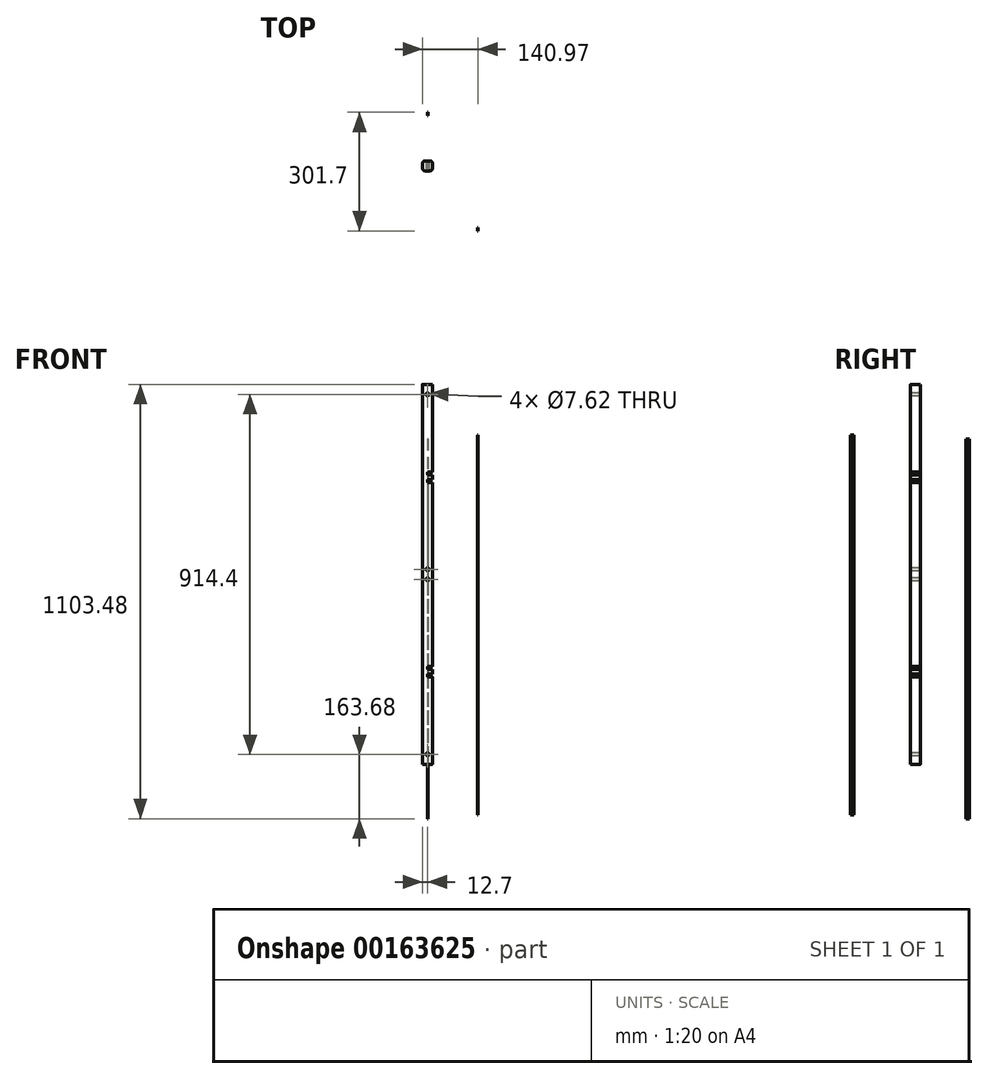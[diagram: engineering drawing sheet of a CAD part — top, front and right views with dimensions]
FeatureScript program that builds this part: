
annotation { "Feature Type Name" : "Feature", "Feature Type Description" : "" }
export const myFeature = defineFeature(function(context is Context, id is Id, definition is map)
    precondition{}
    {
        {
            var Q0;
            Q0=qCreatedBy(makeId("Top.planeOp"),FACE);
            var sketch = newSketch(context, id + "F0", { "sketchPlane" : qUnion([Q0])});
            skLineSegment(sketch, "E0.bottom", {"start": v(6.35, 12.7) * mm, "end": v(-6.35, 12.7) * mm});
            skLineSegment(sketch, "E0.top", {"start": v(6.35, -12.7) * mm, "end": v(-6.35, -12.7) * mm});
            skLineSegment(sketch, "E0.left", {"start": v(12.7, 6.35) * mm, "end": v(12.7, -6.35) * mm});
            skLineSegment(sketch, "E0.right", {"start": v(-12.7, 6.35) * mm, "end": v(-12.7, -6.35) * mm});
            skPoint(sketch, "E0.middle", {"position": v(0, 0) * mm});
            skPoint(sketch, "E1.visualSharp", {"position": v(-12.7, 12.7) * mm});
            skArc(sketch, "E1.filletArc", {"start": v(-6.35, 12.7) * mm, "mid": v(-10.84, 10.84) * mm, "end": v(-12.7, 6.35) * mm});
            skPoint(sketch, "E2.visualSharp", {"position": v(-12.7, -12.7) * mm});
            skArc(sketch, "E2.filletArc", {"start": v(-12.7, -6.35) * mm, "mid": v(-10.84, -10.84) * mm, "end": v(-6.35, -12.7) * mm});
            skPoint(sketch, "E3.visualSharp", {"position": v(12.7, -12.7) * mm});
            skArc(sketch, "E3.filletArc", {"start": v(6.35, -12.7) * mm, "mid": v(10.84, -10.84) * mm, "end": v(12.7, -6.35) * mm});
            skPoint(sketch, "E4.visualSharp", {"position": v(12.7, 12.7) * mm});
            skArc(sketch, "E4.filletArc", {"start": v(12.7, 6.35) * mm, "mid": v(10.84, 10.84) * mm, "end": v(6.35, 12.7) * mm});
            skSolve(sketch);
        }
        {
            var Q0;
            Q0=qSketchRegion(id+"F0",true);
            extrude(context, id + "F1", {"entities" : qUnion([Q0]), "depth" : 965.2 * mm});
        }
        {
            var Q0;
            Q0=qCreatedBy(makeId("Right.planeOp"),FACE);
            var sketch = newSketch(context, id + "F2", { "sketchPlane" : qUnion([Q0])});
            skLineSegment(sketch, "E5.bottom", {"start": v(-165.43, 836.7) * mm, "end": v(-156.96, 836.7) * mm});
            skLineSegment(sketch, "E5.top", {"start": v(-165.43, -128.5) * mm, "end": v(-156.96, -128.5) * mm});
            skLineSegment(sketch, "E5.left", {"start": v(-165.43, 836.7) * mm, "end": v(-165.43, -128.5) * mm});
            skLineSegment(sketch, "E5.right", {"start": v(-156.96, 836.7) * mm, "end": v(-156.96, -128.5) * mm});
            skSolve(sketch);
        }
        {
            var Q0;
            Q0=qSketchRegion(id+"F2",true);
            extrude(context, id + "F3", {"entities" : qUnion([Q0]), "depth" : 1.27 * mm});
        }
        {
            var Q0;
            Q0=qCreatedBy(makeId("Right.planeOp"),FACE);
            var sketch = newSketch(context, id + "F4", { "sketchPlane" : qUnion([Q0])});
            skLineSegment(sketch, "E6.bottom", {"start": v(127.8, 826.92) * mm, "end": v(136.27, 826.92) * mm});
            skLineSegment(sketch, "E6.top", {"start": v(127.8, -138.28) * mm, "end": v(136.27, -138.28) * mm});
            skLineSegment(sketch, "E6.left", {"start": v(127.8, 826.92) * mm, "end": v(127.8, -138.28) * mm});
            skLineSegment(sketch, "E6.right", {"start": v(136.27, 826.92) * mm, "end": v(136.27, -138.28) * mm});
            skSolve(sketch);
        }
        {
            var Q0;
            Q0=qSketchRegion(id+"F4",true);
            extrude(context, id + "F5", {"entities" : qUnion([Q0]), "depth" : 1.27 * mm});
        }
        {
            var Q0;
            Q0=makeQuery(id+"F1.opExtrude","SWEPT_FACE",FACE,{"disambiguationData":[OSD([sQuery(id+"F0.wireOp",EDGE,"E0.left")])]});
            var sketch = newSketch(context, id + "F6", { "sketchPlane" : qUnion([Q0])});
            skLineSegment(sketch, "E7", {"start": v(0, 0) * mm, "end": v(0, 965.2) * mm});
            skLineSegment(sketch, "E8", {"start": v(0, 742.95) * mm, "end": v(12.7, 742.95) * mm});
            skLineSegment(sketch, "E9", {"start": v(0, 723.9) * mm, "end": v(12.7, 723.9) * mm});
            skLineSegment(sketch, "E10", {"start": v(0, 222.25) * mm, "end": v(12.7, 222.25) * mm});
            skLineSegment(sketch, "E11", {"start": v(0, 241.3) * mm, "end": v(12.7, 241.3) * mm});
            skLineSegment(sketch, "E12.bottom", {"start": v(12.7, 222.25) * mm, "end": v(-12.7, 222.25) * mm});
            skLineSegment(sketch, "E12.top", {"start": v(12.7, 229.87) * mm, "end": v(-12.7, 229.87) * mm});
            skLineSegment(sketch, "E12.left", {"start": v(12.7, 222.25) * mm, "end": v(12.7, 229.87) * mm});
            skLineSegment(sketch, "E12.right", {"start": v(-12.7, 222.25) * mm, "end": v(-12.7, 229.87) * mm});
            skLineSegment(sketch, "E13.bottom", {"start": v(12.7, 241.3) * mm, "end": v(-12.7, 241.3) * mm});
            skLineSegment(sketch, "E13.top", {"start": v(12.7, 248.92) * mm, "end": v(-12.7, 248.92) * mm});
            skLineSegment(sketch, "E13.left", {"start": v(12.7, 241.3) * mm, "end": v(12.7, 248.92) * mm});
            skLineSegment(sketch, "E13.right", {"start": v(-12.7, 241.3) * mm, "end": v(-12.7, 248.92) * mm});
            skLineSegment(sketch, "E14.bottom", {"start": v(12.7, 742.95) * mm, "end": v(-12.7, 742.95) * mm});
            skLineSegment(sketch, "E14.top", {"start": v(12.7, 735.33) * mm, "end": v(-12.7, 735.33) * mm});
            skLineSegment(sketch, "E14.left", {"start": v(12.7, 742.95) * mm, "end": v(12.7, 735.33) * mm});
            skLineSegment(sketch, "E14.right", {"start": v(-12.7, 742.95) * mm, "end": v(-12.7, 735.33) * mm});
            skLineSegment(sketch, "E15.bottom", {"start": v(12.7, 723.9) * mm, "end": v(-12.7, 723.9) * mm});
            skLineSegment(sketch, "E15.top", {"start": v(12.7, 716.28) * mm, "end": v(-12.7, 716.28) * mm});
            skLineSegment(sketch, "E15.left", {"start": v(12.7, 723.9) * mm, "end": v(12.7, 716.28) * mm});
            skLineSegment(sketch, "E15.right", {"start": v(-12.7, 723.9) * mm, "end": v(-12.7, 716.28) * mm});
            skSolve(sketch);
        }
        {
            var Q0;
            {var subQ0=sQuery(id+"F6.wireOp",EDGE,"E14.right");Q0=makeQuery(id+"F6.imprint","IMPRINT",FACE,{"disambiguationData":[TD([[makeQuery(id+"F6.imprint","IMPRINT",EDGE,{"derivedFrom":subQ0}),1.0]])]});}
            var Q1;
            {var subQ0=sQuery(id+"F6.wireOp",EDGE,"E14.top");var subQ1=sQuery(id+"F6.wireOp",EDGE,"E7");var subQ2=makeQuery(id+"F6.imprint","INTERSECT",VERTEX,{"derivedFrom":[subQ1,subQ0]});Q1=makeQuery(id+"F6.imprint","IMPRINT",FACE,{"disambiguationData":[TD([[makeQuery(id+"F6.imprint","IMPRINT",EDGE,{"disambiguationData":[TD([[subQ2,-1.0]])],"derivedFrom":subQ1}),1.0]])]});}
            var Q2;
            {var subQ0=sQuery(id+"F6.wireOp",EDGE,"E14.top");var subQ1=sQuery(id+"F6.wireOp",EDGE,"E7");var subQ2=makeQuery(id+"F6.imprint","INTERSECT",VERTEX,{"derivedFrom":[subQ1,subQ0]});Q2=makeQuery(id+"F6.imprint","IMPRINT",FACE,{"disambiguationData":[TD([[makeQuery(id+"F6.imprint","IMPRINT",EDGE,{"disambiguationData":[TD([[subQ2,-1.0]])],"derivedFrom":subQ1}),-1.0]])]});}
            var Q3;
            {var subQ0=sQuery(id+"F6.wireOp",EDGE,"E14.left");Q3=makeQuery(id+"F6.imprint","IMPRINT",FACE,{"disambiguationData":[TD([[makeQuery(id+"F6.imprint","IMPRINT",EDGE,{"derivedFrom":subQ0}),-1.0]])]});}
            var Q4;
            {var subQ0=sQuery(id+"F6.wireOp",EDGE,"E15.left");Q4=makeQuery(id+"F6.imprint","IMPRINT",FACE,{"disambiguationData":[TD([[makeQuery(id+"F6.imprint","IMPRINT",EDGE,{"derivedFrom":subQ0}),-1.0]])]});}
            var Q5;
            {var subQ0=sQuery(id+"F6.wireOp",EDGE,"E15.top");var subQ1=sQuery(id+"F6.wireOp",EDGE,"E7");var subQ2=makeQuery(id+"F6.imprint","INTERSECT",VERTEX,{"derivedFrom":[subQ1,subQ0]});Q5=makeQuery(id+"F6.imprint","IMPRINT",FACE,{"disambiguationData":[TD([[makeQuery(id+"F6.imprint","IMPRINT",EDGE,{"disambiguationData":[TD([[subQ2,-1.0]])],"derivedFrom":subQ1}),-1.0]])]});}
            var Q6;
            {var subQ0=sQuery(id+"F6.wireOp",EDGE,"E15.top");var subQ1=sQuery(id+"F6.wireOp",EDGE,"E7");var subQ2=makeQuery(id+"F6.imprint","INTERSECT",VERTEX,{"derivedFrom":[subQ1,subQ0]});Q6=makeQuery(id+"F6.imprint","IMPRINT",FACE,{"disambiguationData":[TD([[makeQuery(id+"F6.imprint","IMPRINT",EDGE,{"disambiguationData":[TD([[subQ2,-1.0]])],"derivedFrom":subQ1}),1.0]])]});}
            var Q7;
            {var subQ0=sQuery(id+"F6.wireOp",EDGE,"E15.right");Q7=makeQuery(id+"F6.imprint","IMPRINT",FACE,{"disambiguationData":[TD([[makeQuery(id+"F6.imprint","IMPRINT",EDGE,{"derivedFrom":subQ0}),1.0]])]});}
            var Q8;
            Q8=sQuery(id+"F6.wireOp",EDGE,"E14.left");
            var Q9;
            Q9=sQuery(id+"F6.wireOp",EDGE,"E8");
            var Q10;
            Q10=sQuery(id+"F6.wireOp",EDGE,"E14.bottom");
            var Q11;
            Q11=sQuery(id+"F6.wireOp",EDGE,"E14.top");
            var Q12;
            Q12=sQuery(id+"F6.wireOp",EDGE,"E14.right");
            var Q13;
            Q13=sQuery(id+"F6.wireOp",EDGE,"E15.bottom");
            var Q14;
            Q14=sQuery(id+"F6.wireOp",EDGE,"E15.top");
            var Q15;
            Q15=sQuery(id+"F6.wireOp",EDGE,"E15.left");
            var Q16;
            Q16=sQuery(id+"F6.wireOp",EDGE,"E15.right");
            extrude(context, id + "F7", {"entities" : qUnion([Q0, Q1, Q2, Q3, Q4, Q5, Q6, Q7]), "operationType" : NewBodyOperationType.REMOVE, "surfaceEntities" : qUnion([Q8, Q9, Q10, Q11, Q12, Q13, Q14, Q15, Q16]), "oppositeDirection" : true, "depth" : 12.7 * mm});
        }
        {
            var Q0;
            {var subQ0=sQuery(id+"F6.wireOp",EDGE,"E13.right");Q0=makeQuery(id+"F6.imprint","IMPRINT",FACE,{"disambiguationData":[TD([[makeQuery(id+"F6.imprint","IMPRINT",EDGE,{"derivedFrom":subQ0}),-1.0]])]});}
            var Q1;
            {var subQ0=sQuery(id+"F6.wireOp",EDGE,"E13.bottom");var subQ1=sQuery(id+"F6.wireOp",EDGE,"E7");var subQ2=makeQuery(id+"F6.imprint","INTERSECT",VERTEX,{"derivedFrom":[subQ1,subQ0]});Q1=makeQuery(id+"F6.imprint","IMPRINT",FACE,{"disambiguationData":[TD([[makeQuery(id+"F6.imprint","IMPRINT",EDGE,{"disambiguationData":[TD([[subQ2,-1.0]])],"derivedFrom":subQ1}),1.0]])]});}
            var Q2;
            {var subQ0=sQuery(id+"F6.wireOp",EDGE,"E13.bottom");var subQ1=sQuery(id+"F6.wireOp",EDGE,"E7");var subQ2=makeQuery(id+"F6.imprint","INTERSECT",VERTEX,{"derivedFrom":[subQ1,subQ0]});Q2=makeQuery(id+"F6.imprint","IMPRINT",FACE,{"disambiguationData":[TD([[makeQuery(id+"F6.imprint","IMPRINT",EDGE,{"disambiguationData":[TD([[subQ2,-1.0]])],"derivedFrom":subQ1}),-1.0]])]});}
            var Q3;
            {var subQ0=sQuery(id+"F6.wireOp",EDGE,"E13.left");Q3=makeQuery(id+"F6.imprint","IMPRINT",FACE,{"disambiguationData":[TD([[makeQuery(id+"F6.imprint","IMPRINT",EDGE,{"derivedFrom":subQ0}),1.0]])]});}
            var Q4;
            {var subQ0=sQuery(id+"F6.wireOp",EDGE,"E12.left");Q4=makeQuery(id+"F6.imprint","IMPRINT",FACE,{"disambiguationData":[TD([[makeQuery(id+"F6.imprint","IMPRINT",EDGE,{"derivedFrom":subQ0}),1.0]])]});}
            var Q5;
            {var subQ0=sQuery(id+"F6.wireOp",EDGE,"E12.bottom");var subQ1=sQuery(id+"F6.wireOp",EDGE,"E7");var subQ2=makeQuery(id+"F6.imprint","INTERSECT",VERTEX,{"derivedFrom":[subQ1,subQ0]});Q5=makeQuery(id+"F6.imprint","IMPRINT",FACE,{"disambiguationData":[TD([[makeQuery(id+"F6.imprint","IMPRINT",EDGE,{"disambiguationData":[TD([[subQ2,-1.0]])],"derivedFrom":subQ1}),-1.0]])]});}
            var Q6;
            {var subQ0=sQuery(id+"F6.wireOp",EDGE,"E12.bottom");var subQ1=sQuery(id+"F6.wireOp",EDGE,"E7");var subQ2=makeQuery(id+"F6.imprint","INTERSECT",VERTEX,{"derivedFrom":[subQ1,subQ0]});Q6=makeQuery(id+"F6.imprint","IMPRINT",FACE,{"disambiguationData":[TD([[makeQuery(id+"F6.imprint","IMPRINT",EDGE,{"disambiguationData":[TD([[subQ2,-1.0]])],"derivedFrom":subQ1}),1.0]])]});}
            var Q7;
            {var subQ0=sQuery(id+"F6.wireOp",EDGE,"E12.right");Q7=makeQuery(id+"F6.imprint","IMPRINT",FACE,{"disambiguationData":[TD([[makeQuery(id+"F6.imprint","IMPRINT",EDGE,{"derivedFrom":subQ0}),-1.0]])]});}
            extrude(context, id + "F8", {"entities" : qUnion([Q0, Q1, Q2, Q3, Q4, Q5, Q6, Q7]), "operationType" : NewBodyOperationType.REMOVE, "oppositeDirection" : true, "depth" : 12.7 * mm});
        }
        {
            var Q0;
            Q0=makeQuery(id+"F3.opExtrude","SWEPT_BODY",BODY,{"disambiguationData":[OSD([sQuery(id+"F2.wireOp",EDGE,"E5.bottom"),sQuery(id+"F2.wireOp",EDGE,"E5.top"),sQuery(id+"F2.wireOp",EDGE,"E5.left"),sQuery(id+"F2.wireOp",EDGE,"E5.right")])]});
            transform(context, id + "F9", {"entities" : qUnion([Q0]), "transformType" : TransformType.TRANSLATION_3D, "dx" : 127 * mm, "dy" : 0 * mm, "dz" : 0 * mm, "makeCopy" : false});
        }
        {
            var Q0;
            Q0=makeQuery(id+"F1.opExtrude","SWEPT_FACE",FACE,{"disambiguationData":[OSD([sQuery(id+"F0.wireOp",EDGE,"E0.top")])]});
            var sketch = newSketch(context, id + "F10", { "sketchPlane" : qUnion([Q0])});
            skLineSegment(sketch, "E16", {"start": v(0, 965.2) * mm, "end": v(0, 939.8) * mm});
            skLineSegment(sketch, "E17", {"start": v(0, 0) * mm, "end": v(0, 25.4) * mm});
            skCircle(sketch, "E18", {"center": v(0, 469.9) * mm, "radius": 3.81 * mm});
            skCircle(sketch, "E19", {"center": v(0, 495.3) * mm, "radius": 3.81 * mm});
            skCircle(sketch, "E20", {"center": v(0, 939.8) * mm, "radius": 3.81 * mm});
            skCircle(sketch, "E21", {"center": v(0, 25.4) * mm, "radius": 3.81 * mm});
            skSolve(sketch);
        }
        {
            var Q0;
            Q0=makeQuery(id+"F10.imprint","IMPRINT",FACE,{"disambiguationData":[TD([[makeQuery(id+"F10.imprint","IMPRINT",EDGE,{"derivedFrom":sQuery(id+"F10.wireOp",EDGE,"E20")}),1.0]])]});
            var Q1;
            Q1=makeQuery(id+"F10.imprint","IMPRINT",FACE,{"disambiguationData":[TD([[makeQuery(id+"F10.imprint","IMPRINT",EDGE,{"derivedFrom":sQuery(id+"F10.wireOp",EDGE,"E19")}),1.0]])]});
            var Q2;
            Q2=makeQuery(id+"F10.imprint","IMPRINT",FACE,{"disambiguationData":[TD([[makeQuery(id+"F10.imprint","IMPRINT",EDGE,{"derivedFrom":sQuery(id+"F10.wireOp",EDGE,"E18")}),1.0]])]});
            extrude(context, id + "F11", {"entities" : qUnion([Q0, Q1, Q2]), "operationType" : NewBodyOperationType.REMOVE, "oppositeDirection" : true, "depth" : 25.4 * mm});
        }
        {
            var Q0;
            Q0=makeQuery(id+"F10.imprint","IMPRINT",FACE,{"disambiguationData":[TD([[makeQuery(id+"F10.imprint","IMPRINT",EDGE,{"derivedFrom":sQuery(id+"F10.wireOp",EDGE,"E21")}),1.0]])]});
            extrude(context, id + "F12", {"entities" : qUnion([Q0]), "operationType" : NewBodyOperationType.REMOVE, "oppositeDirection" : true, "depth" : 25.4 * mm});
        }
    });
